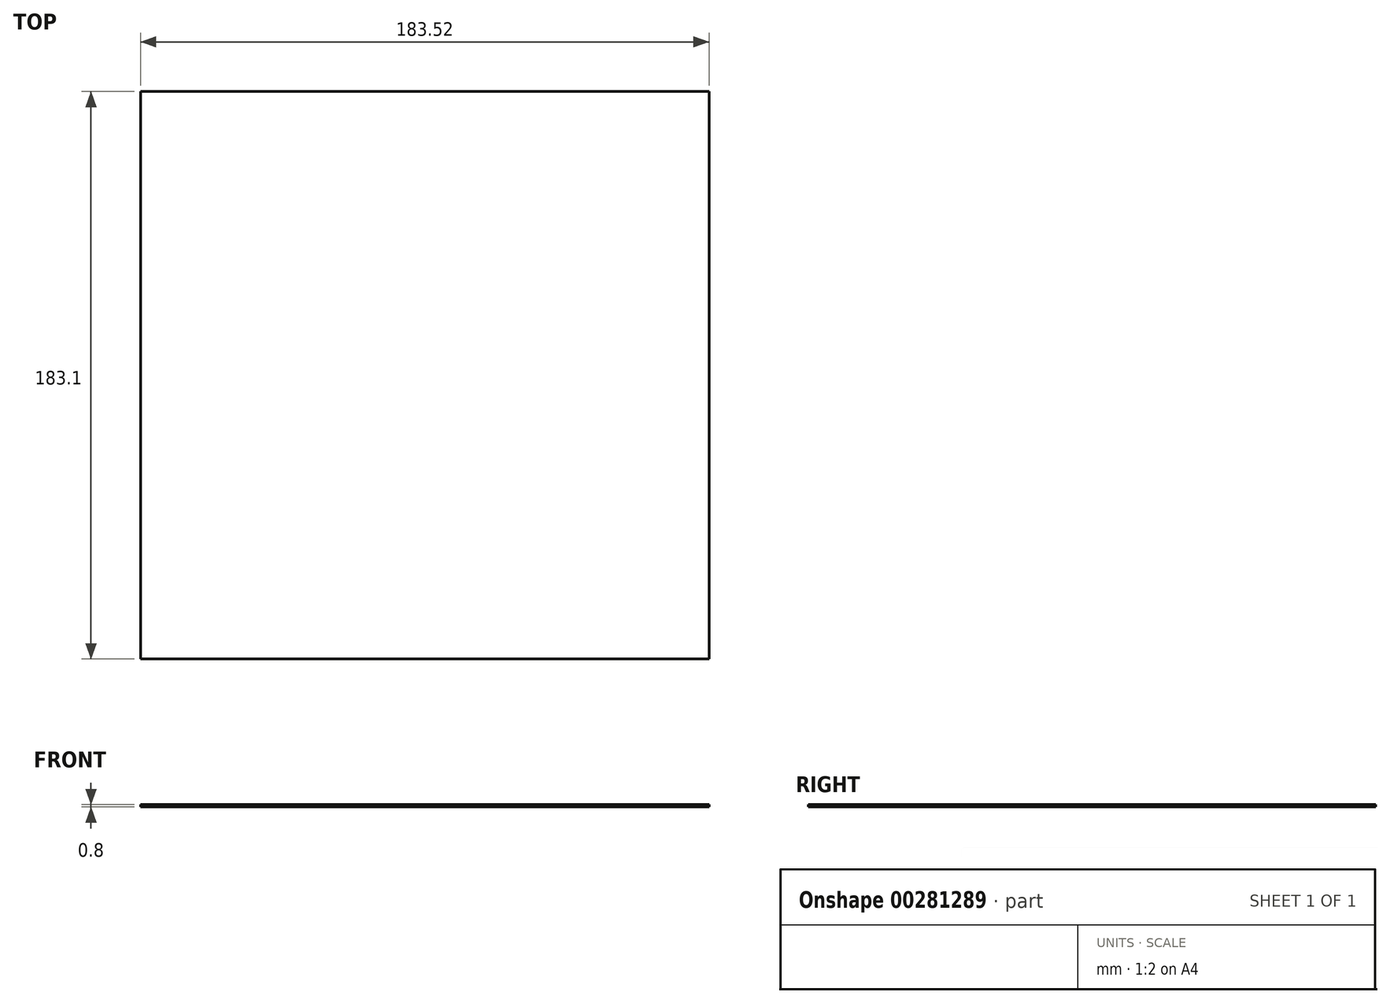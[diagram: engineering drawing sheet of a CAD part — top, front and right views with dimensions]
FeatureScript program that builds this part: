
annotation { "Feature Type Name" : "Feature", "Feature Type Description" : "" }
export const myFeature = defineFeature(function(context is Context, id is Id, definition is map)
    precondition{}
    {
        {
            var Q0;
            Q0=qCreatedBy(makeId("Top.planeOp"),FACE);
            var sketch = newSketch(context, id + "F0", { "sketchPlane" : qUnion([Q0])});
            skLineSegment(sketch, "E0.bottom", {"start": v(91.76, 91.55) * mm, "end": v(-91.76, 91.55) * mm});
            skLineSegment(sketch, "E0.top", {"start": v(91.76, -91.55) * mm, "end": v(-91.76, -91.55) * mm});
            skLineSegment(sketch, "E0.left", {"start": v(91.76, 91.55) * mm, "end": v(91.76, -91.55) * mm});
            skLineSegment(sketch, "E0.right", {"start": v(-91.76, 91.55) * mm, "end": v(-91.76, -91.55) * mm});
            skPoint(sketch, "E0.middle", {"position": v(0, 0) * mm});
            skSolve(sketch);
        }
        {
            var Q0;
            Q0 = qSketchRegion(id + "F0", true);
            extrude(context, id + "F1", {"entities" : qUnion([Q0]), "depth" : .8 * mm});
        }
    });
